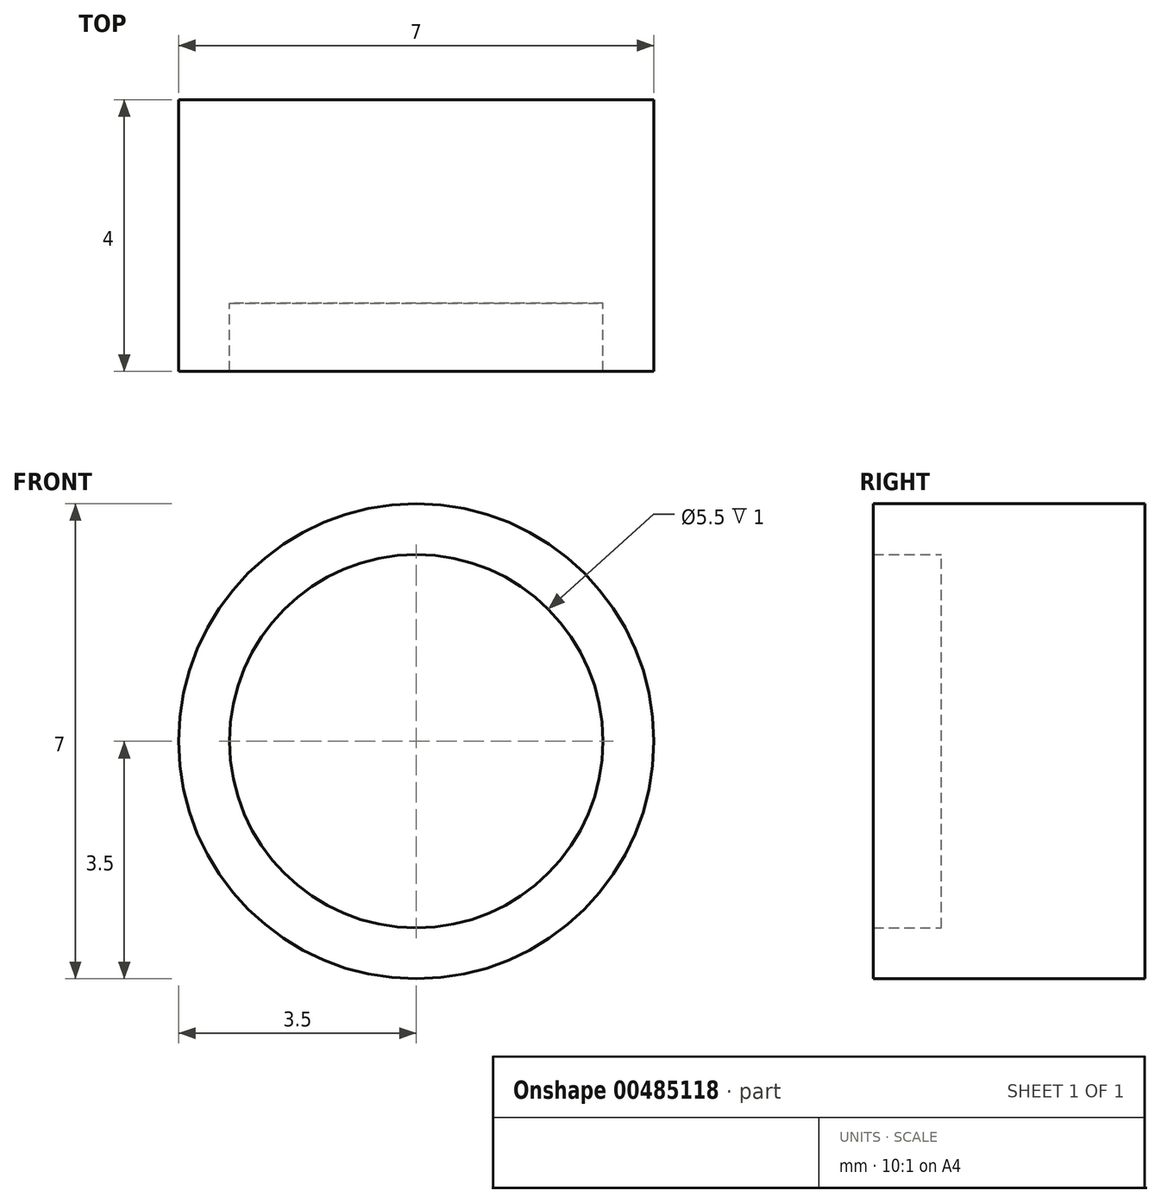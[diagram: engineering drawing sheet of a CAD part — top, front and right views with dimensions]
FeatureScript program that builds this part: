
annotation { "Feature Type Name" : "Feature", "Feature Type Description" : "" }
export const myFeature = defineFeature(function(context is Context, id is Id, definition is map)
    precondition{}
    {
        {
            var Q0;
            Q0=qCreatedBy(makeId("Front.planeOp"),FACE);
            var sketch = newSketch(context, id + "F0", { "sketchPlane" : qUnion([Q0])});
            skCircle(sketch, "E0", {"center": v(0, 0) * mm, "radius": 3.5 * mm});
            skCircle(sketch, "E1", {"center": v(0, 0) * mm, "radius": 2.75 * mm});
            skSolve(sketch);
        }
        {
            var Q0;
            Q0=makeQuery(id+"F0.imprint","IMPRINT",FACE,{"disambiguationData":[TD([[makeQuery(id+"F0.imprint","IMPRINT",EDGE,{"derivedFrom":sQuery(id+"F0.wireOp",EDGE,"E1")}),1.0]])]});
            extrude(context, id + "F1", {"entities" : qUnion([Q0]), "depth" : 3 * mm, "offsetDistance" : 25 * mm});
        }
        {
            var Q0;
            Q0 = qSketchRegion(id + "F0", true);
            extrude(context, id + "F2", {"entities" : qUnion([Q0]), "operationType" : NewBodyOperationType.ADD, "depth" : 4 * mm, "offsetDistance" : 25 * mm});
        }
    });
